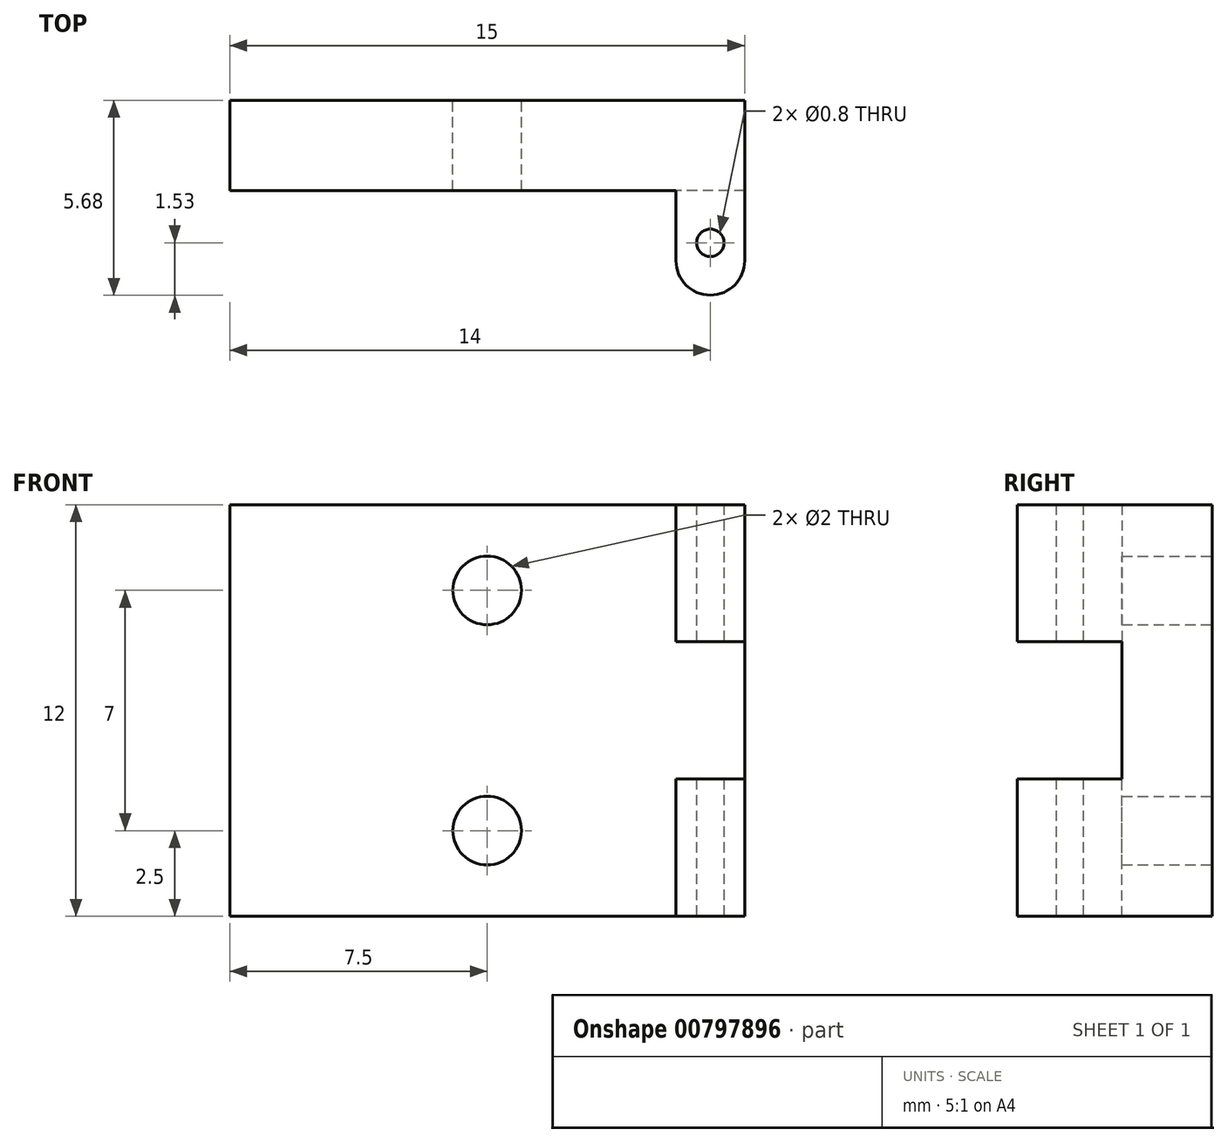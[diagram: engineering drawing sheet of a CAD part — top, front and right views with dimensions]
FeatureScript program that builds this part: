
annotation { "Feature Type Name" : "Feature", "Feature Type Description" : "" }
export const myFeature = defineFeature(function(context is Context, id is Id, definition is map)
    precondition{}
    {
        {
            var Q0;
            Q0=qCreatedBy(makeId("Front.planeOp"),FACE);
            var sketch = newSketch(context, id + "F0", { "sketchPlane" : qUnion([Q0])});
            skLineSegment(sketch, "E0.bottom", {"start": v(7.5, 6) * mm, "end": v(-7.5, 6) * mm});
            skLineSegment(sketch, "E0.top", {"start": v(7.5, -6) * mm, "end": v(-7.5, -6) * mm});
            skLineSegment(sketch, "E0.left", {"start": v(7.5, 6) * mm, "end": v(7.5, -6) * mm});
            skLineSegment(sketch, "E0.right", {"start": v(-7.5, 6) * mm, "end": v(-7.5, -6) * mm});
            skPoint(sketch, "E0.middle", {"position": v(0, 0) * mm});
            skSolve(sketch);
        }
        {
            var Q0;
            Q0=qSketchRegion(id+"F0",true);
            extrude(context, id + "F1", {"entities" : qUnion([Q0]), "depth" : 2.62 * mm, "offsetDistance" : 25 * mm});
        }
        {
            var Q0;
            Q0=makeQuery(id+"F1.opExtrude","CAP_FACE",FACE,{"disambiguationData":[OSD([sQuery(id+"F0.wireOp",EDGE,"E0.bottom"),sQuery(id+"F0.wireOp",EDGE,"E0.top"),sQuery(id+"F0.wireOp",EDGE,"E0.left"),sQuery(id+"F0.wireOp",EDGE,"E0.right")])],"isStart":false});
            var sketch = newSketch(context, id + "F2", { "sketchPlane" : qUnion([Q0])});
            skLineSegment(sketch, "E1.bottom", {"start": v(7.5, 6) * mm, "end": v(5.5, 6) * mm});
            skLineSegment(sketch, "E1.top", {"start": v(7.5, 2) * mm, "end": v(5.5, 2) * mm});
            skLineSegment(sketch, "E1.left", {"start": v(7.5, 6) * mm, "end": v(7.5, 2) * mm});
            skLineSegment(sketch, "E1.right", {"start": v(5.5, 6) * mm, "end": v(5.5, 2) * mm});
            skLineSegment(sketch, "E2.bottom", {"start": v(7.5, -6) * mm, "end": v(5.5, -6) * mm});
            skLineSegment(sketch, "E2.top", {"start": v(7.5, -2) * mm, "end": v(5.5, -2) * mm});
            skLineSegment(sketch, "E2.left", {"start": v(7.5, -6) * mm, "end": v(7.5, -2) * mm});
            skLineSegment(sketch, "E2.right", {"start": v(5.5, -6) * mm, "end": v(5.5, -2) * mm});
            skSolve(sketch);
        }
        {
            var Q0;
            Q0=qSketchRegion(id+"F2",true);
            extrude(context, id + "F3", {"entities" : qUnion([Q0]), "operationType" : NewBodyOperationType.ADD, "depth" : 3.05 * mm, "offsetDistance" : 25 * mm});
        }
        {
            var Q0;
            Q0=makeQuery(id+"F3.boolean.opBoolean","MERGE",FACE,{"derivedFrom":[makeQuery(id+"F1.opExtrude","SWEPT_FACE",FACE,{"disambiguationData":[OSD([sQuery(id+"F0.wireOp",EDGE,"E0.top")])]}),makeQuery(id+"F3.opExtrude","SWEPT_FACE",FACE,{"disambiguationData":[OSD([sQuery(id+"F2.wireOp",EDGE,"E2.bottom")])]})]});
            var sketch = newSketch(context, id + "F4", { "sketchPlane" : qUnion([Q0])});
            skLineSegment(sketch, "E3.bottom", {"start": v(5.5, 5.67) * mm, "end": v(7.5, 5.67) * mm, "construction": true});
            skLineSegment(sketch, "E3.top", {"start": v(5.5, 2.62) * mm, "end": v(7.5, 2.62) * mm, "construction": true});
            skLineSegment(sketch, "E3.left", {"start": v(5.5, 5.67) * mm, "end": v(5.5, 2.62) * mm, "construction": true});
            skLineSegment(sketch, "E3.right", {"start": v(7.5, 5.67) * mm, "end": v(7.5, 2.62) * mm, "construction": true});
            skLineSegment(sketch, "E4", {"start": v(5.5, 5.67) * mm, "end": v(7.5, 2.62) * mm, "construction": true});
            skCircle(sketch, "E5", {"center": v(6.5, 4.15) * mm, "radius": 0.4 * mm});
            skSolve(sketch);
        }
        {
            var Q0;
            Q0=qSketchRegion(id+"F4",true);
            extrude(context, id + "F5", {"entities" : qUnion([Q0]), "operationType" : NewBodyOperationType.REMOVE, "oppositeDirection" : true, "depth" : 25 * mm, "offsetDistance" : 25 * mm});
        }
        {
            var Q0;
            Q0=makeQuery(id+"F3.opExtrude","CAP_EDGE",EDGE,{"disambiguationData":[OSD([sQuery(id+"F2.wireOp",EDGE,"E1.left")])],"isStart":false});
            var Q1;
            Q1=makeQuery(id+"F3.opExtrude","CAP_EDGE",EDGE,{"disambiguationData":[OSD([sQuery(id+"F2.wireOp",EDGE,"E1.right")])],"isStart":false});
            var Q2;
            Q2=makeQuery(id+"F3.opExtrude","CAP_EDGE",EDGE,{"disambiguationData":[OSD([sQuery(id+"F2.wireOp",EDGE,"E2.left")])],"isStart":false});
            var Q3;
            Q3=makeQuery(id+"F3.opExtrude","CAP_EDGE",EDGE,{"disambiguationData":[OSD([sQuery(id+"F2.wireOp",EDGE,"E2.right")])],"isStart":false});
            fillet(context, id + "F6", {"entities" : qUnion([Q0, Q1, Q2, Q3]), "radius" : 1 * mm, "tangentPropagation" : true, "allowEdgeOverflow" : false});
        }
        {
            var Q0;
            Q0=makeQuery(id+"F1.opExtrude","CAP_FACE",FACE,{"disambiguationData":[OSD([sQuery(id+"F0.wireOp",EDGE,"E0.bottom"),sQuery(id+"F0.wireOp",EDGE,"E0.top"),sQuery(id+"F0.wireOp",EDGE,"E0.left"),sQuery(id+"F0.wireOp",EDGE,"E0.right")])],"isStart":true});
            var sketch = newSketch(context, id + "F7", { "sketchPlane" : qUnion([Q0])});
            skLineSegment(sketch, "E6", {"start": v(0, -3.5) * mm, "end": v(0, 3.5) * mm, "construction": true});
            skCircle(sketch, "E7", {"center": v(0, 3.5) * mm, "radius": 1 * mm});
            skCircle(sketch, "E8", {"center": v(0, -3.5) * mm, "radius": 1 * mm});
            skSolve(sketch);
        }
        {
            var Q0;
            Q0=qSketchRegion(id+"F7",true);
            extrude(context, id + "F8", {"entities" : qUnion([Q0]), "operationType" : NewBodyOperationType.REMOVE, "oppositeDirection" : true, "depth" : 25 * mm, "offsetDistance" : 25 * mm});
        }
    });
